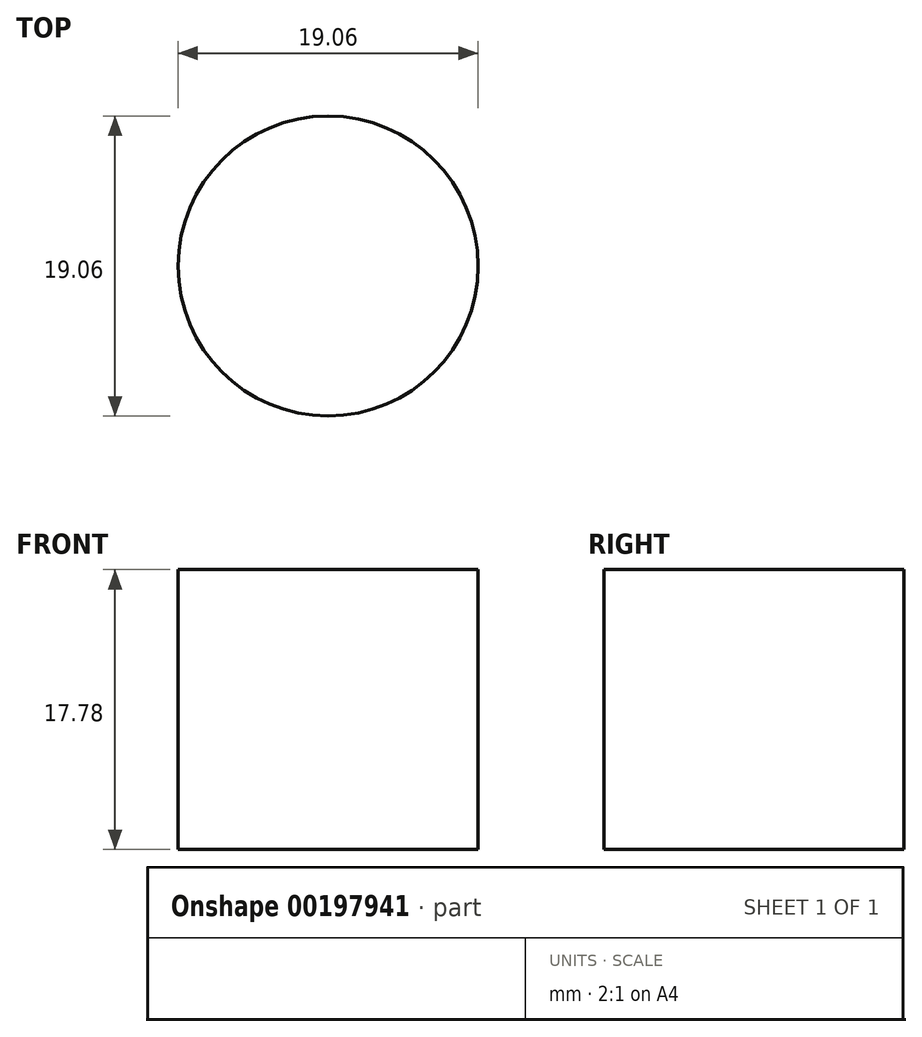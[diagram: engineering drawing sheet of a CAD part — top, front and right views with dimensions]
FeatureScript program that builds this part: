
annotation { "Feature Type Name" : "Feature", "Feature Type Description" : "" }
export const myFeature = defineFeature(function(context is Context, id is Id, definition is map)
    precondition{}
    {
        {
            var Q0;
            Q0=qCreatedBy(makeId("Top.planeOp"),FACE);
            var sketch = newSketch(context, id + "F0", { "sketchPlane" : qUnion([Q0])});
            skCircle(sketch, "E0", {"center": v(0, 0) * mm, "radius": 9.52 * mm});
            skSolve(sketch);
        }
        {
            var Q0;
            Q0=makeQuery(id+"F0.imprint","IMPRINT",FACE,{"disambiguationData":[TD([[makeQuery(id+"F0.imprint","IMPRINT",EDGE,{"derivedFrom":sQuery(id+"F0.wireOp",EDGE,"E0")}),1.0]])]});
            extrude(context, id + "F1", {"entities" : qUnion([Q0]), "depth" : 17.78 * mm});
        }
    });
